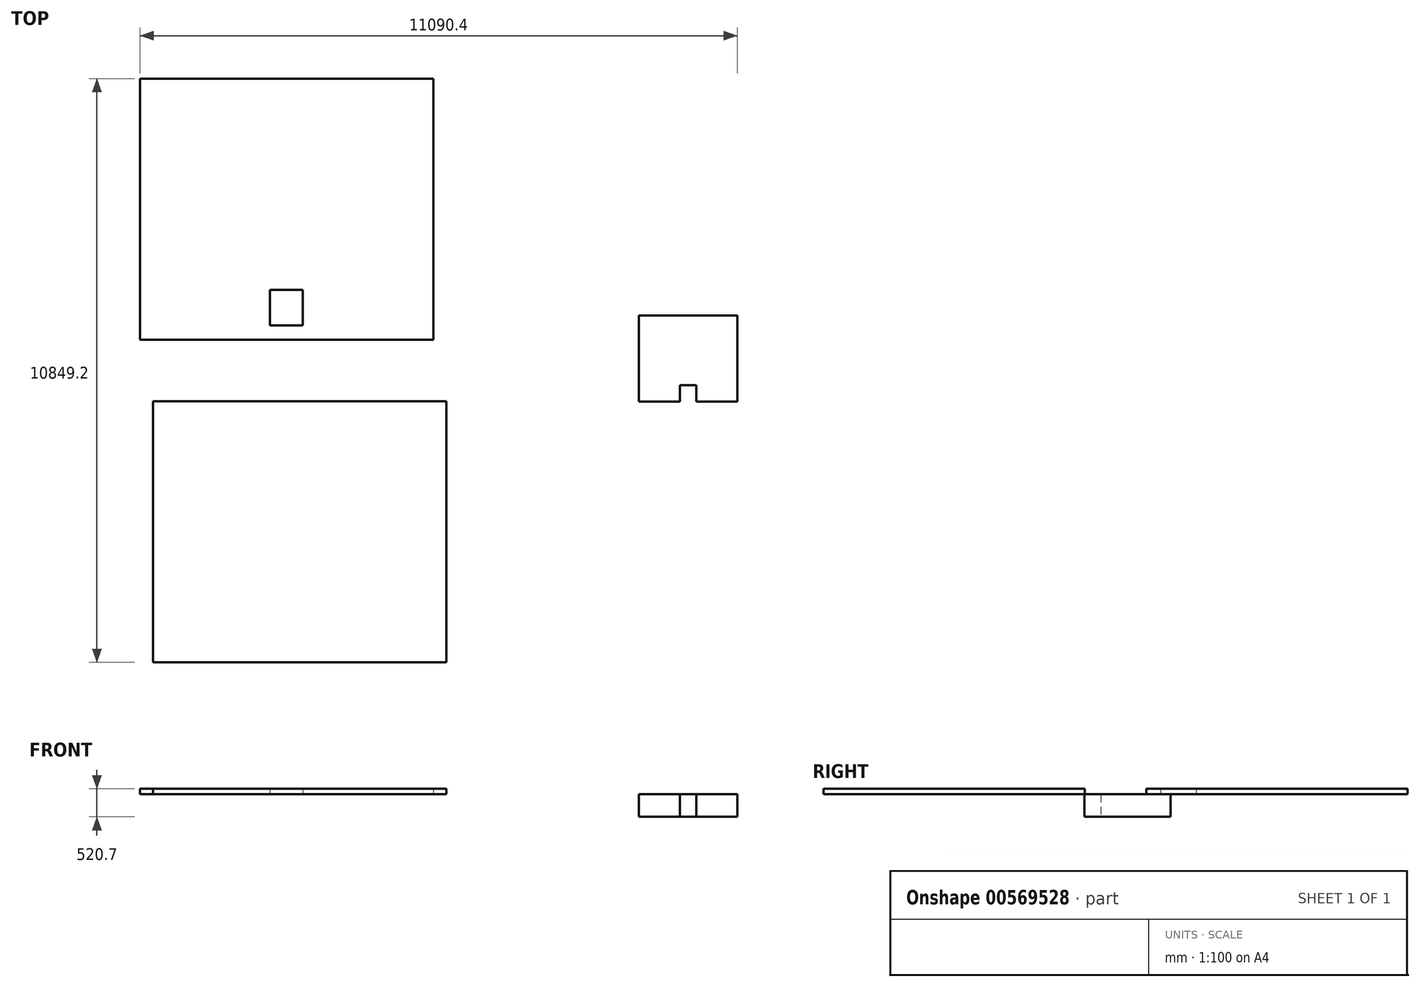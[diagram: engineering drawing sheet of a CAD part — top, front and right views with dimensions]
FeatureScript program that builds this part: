
annotation { "Feature Type Name" : "Feature", "Feature Type Description" : "" }
export const myFeature = defineFeature(function(context is Context, id is Id, definition is map)
    precondition{}
    {
        {
            var Q0;
            Q0=qCreatedBy(makeId("Top.planeOp"),FACE);
            var sketch = newSketch(context, id + "F0", { "sketchPlane" : qUnion([Q0])});
            skLineSegment(sketch, "E0.bottom", {"start": v(-905.13, 969.82) * mm, "end": v(923.67, 969.82) * mm});
            skLineSegment(sketch, "E0.top", {"start": v(-905.13, -630.38) * mm, "end": v(923.67, -630.38) * mm});
            skLineSegment(sketch, "E0.left", {"start": v(-905.13, 969.82) * mm, "end": v(-905.13, -630.38) * mm});
            skLineSegment(sketch, "E0.right", {"start": v(923.67, 969.82) * mm, "end": v(923.67, -630.38) * mm});
            skLineSegment(sketch, "E1.bottom", {"start": v(-143.13, -630.38) * mm, "end": v(161.67, -630.38) * mm});
            skLineSegment(sketch, "E1.top", {"start": v(-143.13, -325.58) * mm, "end": v(161.67, -325.58) * mm});
            skLineSegment(sketch, "E1.left", {"start": v(-143.13, -630.38) * mm, "end": v(-143.13, -325.58) * mm});
            skLineSegment(sketch, "E1.right", {"start": v(161.67, -630.38) * mm, "end": v(161.67, -325.58) * mm});
            skSolve(sketch);
        }
        {
            var Q0;
            Q0=makeQuery(id+"F0.imprint","IMPRINT",FACE,{"disambiguationData":[TD([[makeQuery(id+"F0.imprint","IMPRINT",EDGE,{"derivedFrom":sQuery(id+"F0.wireOp",EDGE,"E0.bottom")}),-1.0]])]});
            extrude(context, id + "F1", {"entities" : qUnion([Q0]), "depth" : 419.1 * mm, "offsetDistance" : 25.4 * mm});
        }
        {
            var Q0;
            Q0=makeQuery(id+"F1.opExtrude","CAP_FACE",FACE,{"disambiguationData":[OSD([sQuery(id+"F0.wireOp",EDGE,"E0.bottom"),sQuery(id+"F0.wireOp",EDGE,"E0.top"),sQuery(id+"F0.wireOp",EDGE,"E0.left"),sQuery(id+"F0.wireOp",EDGE,"E0.right")])],"isStart":false});
            var sketch = newSketch(context, id + "F2", { "sketchPlane" : qUnion([Q0])});
            skLineSegment(sketch, "E2.bottom", {"start": v(-4718.39, 522.5) * mm, "end": v(-10166.69, 522.5) * mm});
            skLineSegment(sketch, "E2.top", {"start": v(-4718.39, 5373.9) * mm, "end": v(-10166.69, 5373.9) * mm});
            skLineSegment(sketch, "E2.left", {"start": v(-4718.39, 522.5) * mm, "end": v(-4718.39, 5373.9) * mm});
            skLineSegment(sketch, "E2.right", {"start": v(-10166.69, 522.5) * mm, "end": v(-10166.69, 5373.9) * mm});
            skLineSegment(sketch, "E3.bottom", {"start": v(-7753.69, 522.5) * mm, "end": v(-7144.09, 522.5) * mm});
            skLineSegment(sketch, "E4.bottom", {"start": v(-7753.69, 1449.6) * mm, "end": v(-7144.09, 1449.6) * mm});
            skLineSegment(sketch, "E4.top", {"start": v(-7753.69, 789.2) * mm, "end": v(-7144.09, 789.2) * mm});
            skLineSegment(sketch, "E4.left", {"start": v(-7753.69, 1449.6) * mm, "end": v(-7753.69, 789.2) * mm});
            skLineSegment(sketch, "E4.right", {"start": v(-7144.09, 1449.6) * mm, "end": v(-7144.09, 789.2) * mm});
            skSolve(sketch);
        }
        {
            var Q0;
            Q0=makeQuery(id+"F2.imprint","IMPRINT",FACE,{"disambiguationData":[TD([[makeQuery(id+"F2.imprint","IMPRINT",EDGE,{"derivedFrom":sQuery(id+"F2.wireOp",EDGE,"E2.bottom")}),-1.0]])]});
            var Q1;
            Q1=sQuery(id+"F2.wireOp",EDGE,"E2.right");
            var Q2;
            Q2=sQuery(id+"F2.wireOp",EDGE,"E2.left");
            var Q3;
            Q3=sQuery(id+"F2.wireOp",EDGE,"E2.bottom");
            var Q4;
            Q4=sQuery(id+"F2.wireOp",EDGE,"E2.top");
            extrude(context, id + "F3", {"entities" : qUnion([Q0]), "surfaceEntities" : qUnion([Q1, Q2, Q3, Q4]), "depth" : 101.6 * mm, "offsetDistance" : 25.4 * mm});
        }
        {
            var Q0;
            Q0=makeQuery(id+"F1.opExtrude","CAP_FACE",FACE,{"disambiguationData":[OSD([sQuery(id+"F0.wireOp",EDGE,"E0.bottom"),sQuery(id+"F0.wireOp",EDGE,"E0.top"),sQuery(id+"F0.wireOp",EDGE,"E0.left"),sQuery(id+"F0.wireOp",EDGE,"E0.right")])],"isStart":false});
            var sketch = newSketch(context, id + "F4", { "sketchPlane" : qUnion([Q0])});
            skLineSegment(sketch, "E5.bottom", {"start": v(-9928.66, -623.88) * mm, "end": v(-4480.36, -623.88) * mm});
            skLineSegment(sketch, "E5.top", {"start": v(-9928.66, -5475.28) * mm, "end": v(-4480.36, -5475.28) * mm});
            skLineSegment(sketch, "E5.left", {"start": v(-9928.66, -623.88) * mm, "end": v(-9928.66, -5475.28) * mm});
            skLineSegment(sketch, "E5.right", {"start": v(-4480.36, -623.88) * mm, "end": v(-4480.36, -5475.28) * mm});
            skSolve(sketch);
        }
        {
            var Q0;
            Q0=makeQuery(id+"F4.imprint","IMPRINT",FACE,{"disambiguationData":[TD([[makeQuery(id+"F4.imprint","IMPRINT",EDGE,{"derivedFrom":sQuery(id+"F4.wireOp",EDGE,"E5.bottom")}),-1.0]])]});
            var Q1;
            Q1=sQuery(id+"F4.wireOp",EDGE,"E5.left");
            var Q2;
            Q2=sQuery(id+"F4.wireOp",EDGE,"E5.bottom");
            var Q3;
            Q3=sQuery(id+"F4.wireOp",EDGE,"E5.right");
            var Q4;
            Q4=sQuery(id+"F4.wireOp",EDGE,"E5.top");
            extrude(context, id + "F5", {"entities" : qUnion([Q0]), "surfaceEntities" : qUnion([Q1, Q2, Q3, Q4]), "depth" : 101.6 * mm, "offsetDistance" : 25.4 * mm});
        }
    });
